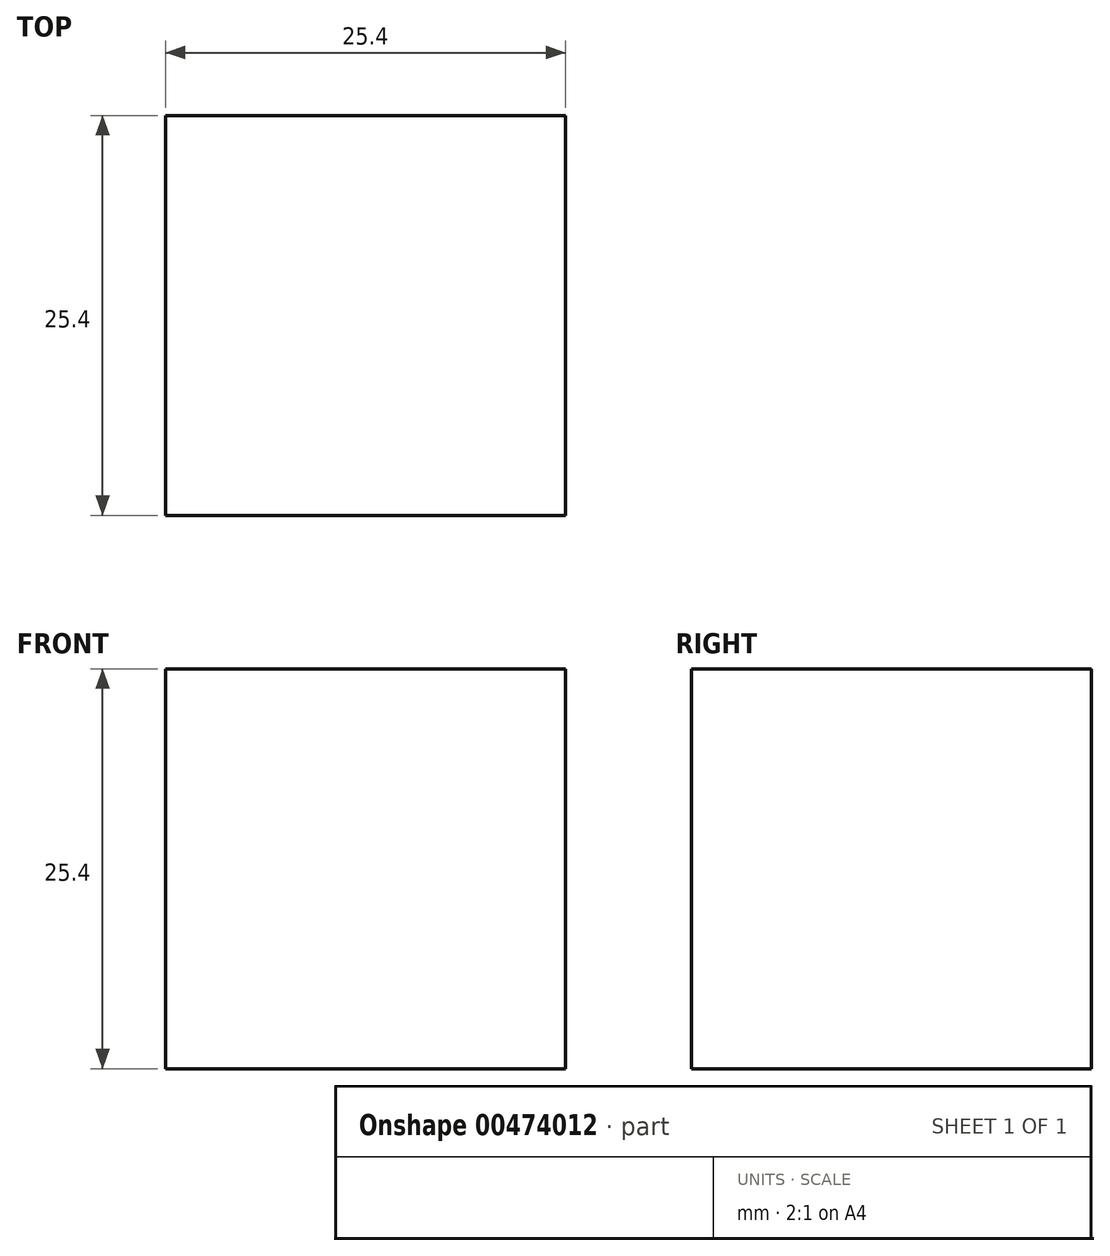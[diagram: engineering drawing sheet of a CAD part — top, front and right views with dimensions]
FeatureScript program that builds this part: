
annotation { "Feature Type Name" : "Feature", "Feature Type Description" : "" }
export const myFeature = defineFeature(function(context is Context, id is Id, definition is map)
    precondition{}
    {
        {
            var Q0;
            Q0=qCreatedBy(makeId("Top.planeOp"),FACE);
            var sketch = newSketch(context, id + "F0", { "sketchPlane" : qUnion([Q0])});
            skLineSegment(sketch, "E0", {"start": v(-25.4, 0) * mm, "end": v(0, 0) * mm});
            skLineSegment(sketch, "E1", {"start": v(-25.4, 0) * mm, "end": v(-25.4, -25.4) * mm});
            skLineSegment(sketch, "E2", {"start": v(-25.4, -25.4) * mm, "end": v(0, -25.4) * mm});
            skLineSegment(sketch, "E3", {"start": v(0, -25.4) * mm, "end": v(0, 0) * mm});
            skSolve(sketch);
        }
        {
            var Q0;
            Q0 = qSketchRegion(id + "F0", true);
            extrude(context, id + "F1", {"entities" : qUnion([Q0]), "depth" : 25.4 * mm});
        }
    });
